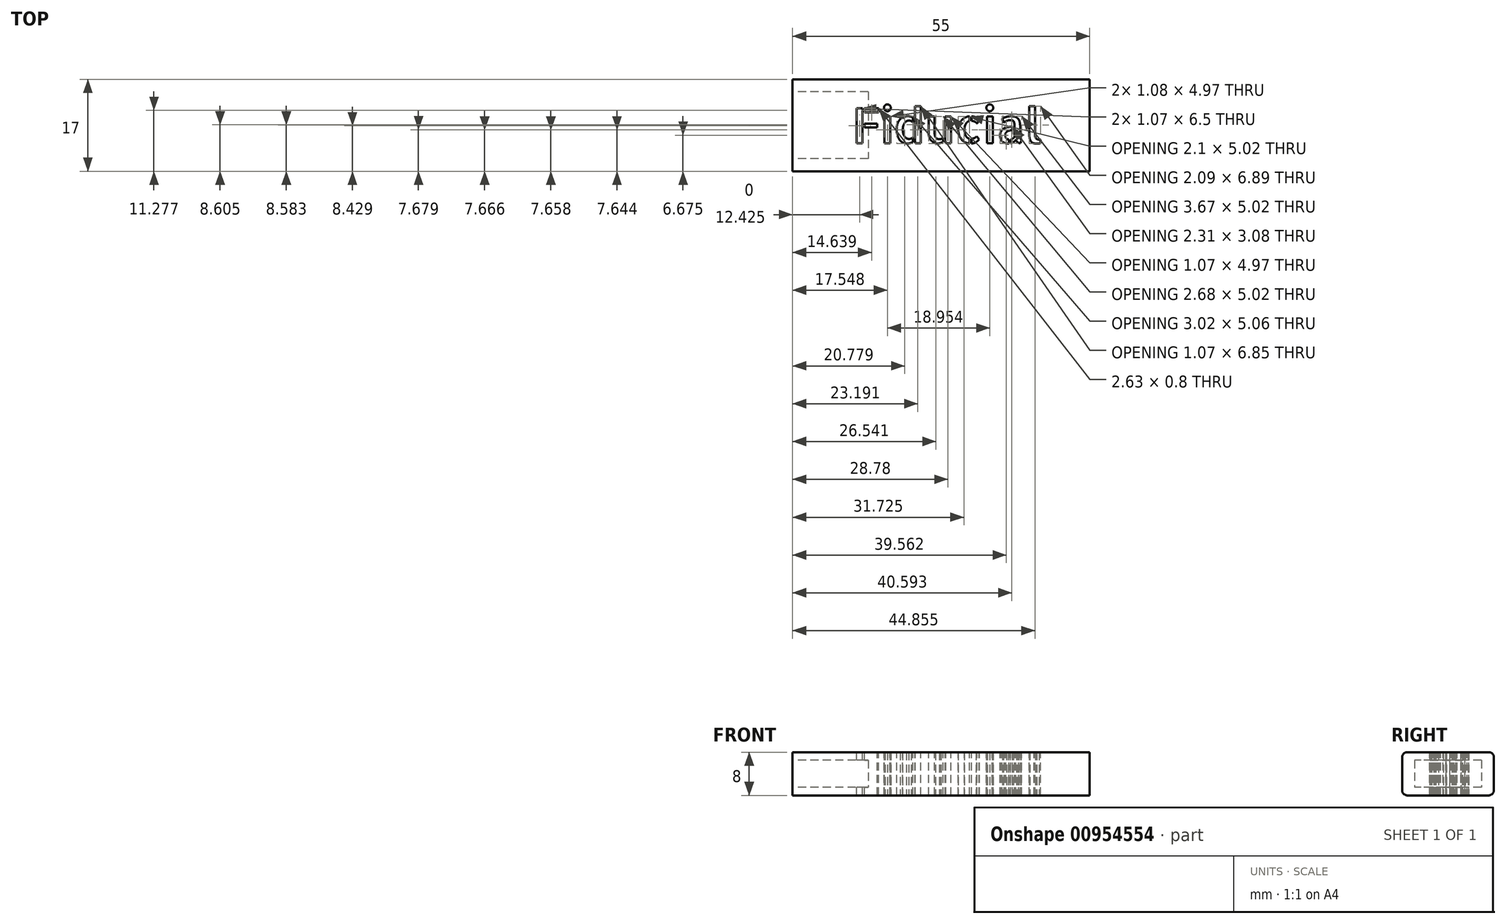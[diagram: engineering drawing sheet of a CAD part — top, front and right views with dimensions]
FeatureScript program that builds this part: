
annotation { "Feature Type Name" : "Feature", "Feature Type Description" : "" }
export const myFeature = defineFeature(function(context is Context, id is Id, definition is map)
    precondition{}
    {
        {
            var Q0;
            Q0=qCreatedBy(makeId("Front.planeOp"),FACE);
            var sketch = newSketch(context, id + "F0", { "sketchPlane" : qUnion([Q0])});
            skLineSegment(sketch, "E0.bottom", {"start": v(-7.5, 4) * mm, "end": v(7.5, 4) * mm});
            skLineSegment(sketch, "E0.top", {"start": v(-7.5, -4) * mm, "end": v(7.5, -4) * mm});
            skLineSegment(sketch, "E0.left", {"start": v(-8.5, 3) * mm, "end": v(-8.5, -3) * mm});
            skLineSegment(sketch, "E0.right", {"start": v(8.5, 3) * mm, "end": v(8.5, -3) * mm});
            skPoint(sketch, "E1.visualSharp", {"position": v(-8.5, 4) * mm});
            skArc(sketch, "E1.filletArc", {"start": v(-7.5, 4) * mm, "mid": v(-8.2, 3.7) * mm, "end": v(-8.5, 3) * mm});
            skPoint(sketch, "E2.visualSharp", {"position": v(8.5, 4) * mm});
            skArc(sketch, "E2.filletArc", {"start": v(8.5, 3) * mm, "mid": v(8.2, 3.7) * mm, "end": v(7.5, 4) * mm});
            skPoint(sketch, "E3.visualSharp", {"position": v(8.5, -4) * mm});
            skArc(sketch, "E3.filletArc", {"start": v(7.5, -4) * mm, "mid": v(8.2, -3.7) * mm, "end": v(8.5, -3) * mm});
            skPoint(sketch, "E4.visualSharp", {"position": v(-8.5, -4) * mm});
            skArc(sketch, "E4.filletArc", {"start": v(-8.5, -3) * mm, "mid": v(-8.2, -3.7) * mm, "end": v(-7.5, -4) * mm});
            skSolve(sketch);
        }
        {
            var Q0;
            Q0 = qSketchRegion(id + "F0", true);
            extrude(context, id + "F1", {"entities" : qUnion([Q0]), "depth" : 55 * mm, "offsetDistance" : 25 * mm});
        }
        {
            var Q0;
            Q0=makeQuery(id+"F1.opExtrude","CAP_FACE",FACE,{"disambiguationData":[OSD([sQuery(id+"F0.wireOp",EDGE,"E0.bottom"),sQuery(id+"F0.wireOp",EDGE,"E0.top"),sQuery(id+"F0.wireOp",EDGE,"E0.left"),sQuery(id+"F0.wireOp",EDGE,"E0.right"),sQuery(id+"F0.wireOp",EDGE,"E1.filletArc"),sQuery(id+"F0.wireOp",EDGE,"E2.filletArc"),sQuery(id+"F0.wireOp",EDGE,"E3.filletArc"),sQuery(id+"F0.wireOp",EDGE,"E4.filletArc")])],"isStart":false});
            var sketch = newSketch(context, id + "F2", { "sketchPlane" : qUnion([Q0])});
            skLineSegment(sketch, "E5.bottom", {"start": v(-6.2, 2.5) * mm, "end": v(6.2, 2.5) * mm});
            skLineSegment(sketch, "E5.top", {"start": v(-6.2, -2.5) * mm, "end": v(6.2, -2.5) * mm});
            skLineSegment(sketch, "E5.left", {"start": v(-6.2, 2.5) * mm, "end": v(-6.2, -2.5) * mm});
            skLineSegment(sketch, "E5.right", {"start": v(6.2, 2.5) * mm, "end": v(6.2, -2.5) * mm});
            skPoint(sketch, "E5.middle", {"position": v(0, 0) * mm});
            skSolve(sketch);
        }
        {
            var Q0;
            Q0=makeQuery(id+"F2.imprint","IMPRINT",FACE,{"disambiguationData":[TD([[makeQuery(id+"F2.imprint","IMPRINT",EDGE,{"derivedFrom":sQuery(id+"F2.wireOp",EDGE,"E5.bottom")}),-1.0]])]});
            extrude(context, id + "F3", {"entities" : qUnion([Q0]), "operationType" : NewBodyOperationType.REMOVE, "oppositeDirection" : true, "depth" : 14 * mm, "offsetDistance" : 25 * mm});
        }
        {
            var Q0;
            Q0=makeQuery(id+"F1.opExtrude","SWEPT_BODY",BODY,{"disambiguationData":[OSD([sQuery(id+"F0.wireOp",EDGE,"E0.bottom"),sQuery(id+"F0.wireOp",EDGE,"E0.top"),sQuery(id+"F0.wireOp",EDGE,"E0.left"),sQuery(id+"F0.wireOp",EDGE,"E0.right"),sQuery(id+"F0.wireOp",EDGE,"E1.filletArc"),sQuery(id+"F0.wireOp",EDGE,"E2.filletArc"),sQuery(id+"F0.wireOp",EDGE,"E3.filletArc"),sQuery(id+"F0.wireOp",EDGE,"E4.filletArc")])]});
            var Q1;
            Q1=makeQuery(id+"F1.opExtrude","CAP_EDGE",EDGE,{"disambiguationData":[OSD([sQuery(id+"F0.wireOp",EDGE,"E0.right")])],"isStart":true});
            transform(context, id + "F4", {"entities" : qUnion([Q0]), "transformType" : TransformType.ROTATION, "transformAxis" : qUnion([Q1]), "angle" : 90 * degree, "makeCopy" : false});
        }
        {
            var Q0;
            Q0=makeQuery(id+"F1.opExtrude","SWEPT_FACE",FACE,{"disambiguationData":[OSD([sQuery(id+"F0.wireOp",EDGE,"E0.bottom")])]});
            var sketch = newSketch(context, id + "F5", { "sketchPlane" : qUnion([Q0])});
            skText(sketch, "E6", { "text": "Fiducial", "fontName": "AllertaStencil-Regular.ttf"});
            const initialGuessF5  = {"E6": [-0.03545, 0.00518, 1, 0, 0.0065]};
            skSetInitialGuess(sketch, initialGuessF5);
            skSolve(sketch);
        }
        {
            var Q0;
            Q0 = qSketchRegion(id + "F5", true);
            extrude(context, id + "F6", {"entities" : qUnion([Q0]), "operationType" : NewBodyOperationType.REMOVE, "oppositeDirection" : true, "depth" : 10 * mm, "offsetDistance" : 25 * mm});
        }
    });
